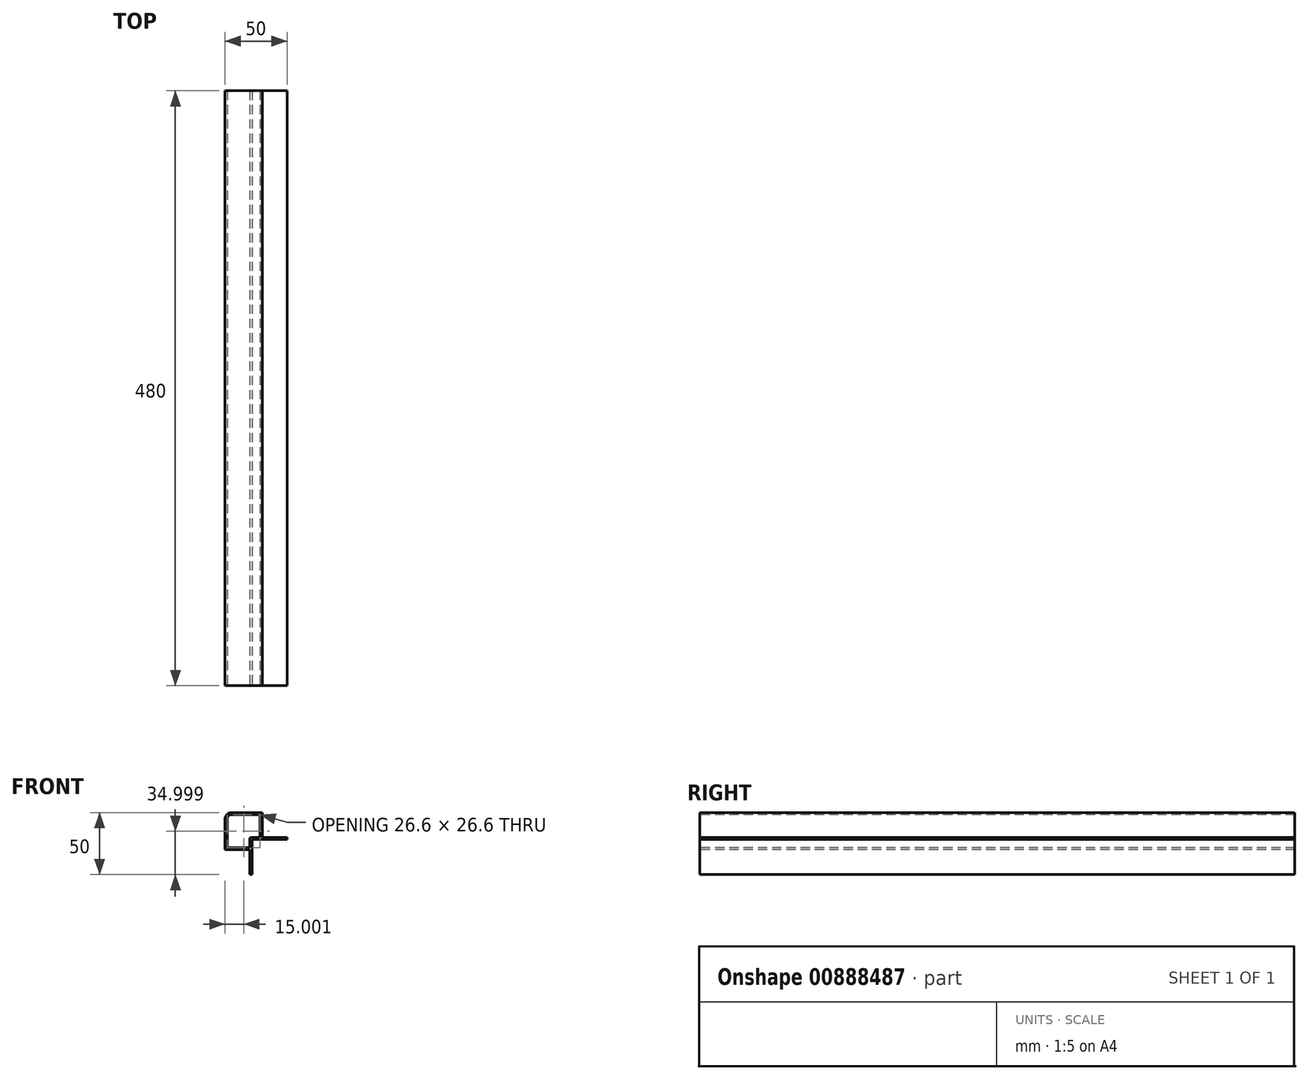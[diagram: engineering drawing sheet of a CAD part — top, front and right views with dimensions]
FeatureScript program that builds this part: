
annotation { "Feature Type Name" : "Feature", "Feature Type Description" : "" }
export const myFeature = defineFeature(function(context is Context, id is Id, definition is map)
    precondition{}
    {
        {
            var Q0;
            Q0=qCreatedBy(makeId("Front.planeOp"),FACE);
            var sketch = newSketch(context, id + "F0", { "sketchPlane" : qUnion([Q0])});
            skLineSegment(sketch, "E0.bottom", {"start": v(-14.05, 19.05) * mm, "end": v(10.95, 19.05) * mm});
            skLineSegment(sketch, "E0.top", {"start": v(-19.05, -10.95) * mm, "end": v(0.95, -10.95) * mm});
            skLineSegment(sketch, "E0.left", {"start": v(-19.05, 14.05) * mm, "end": v(-19.05, -10.95) * mm});
            skLineSegment(sketch, "E0.right", {"start": v(10.95, 19.05) * mm, "end": v(10.95, -0.95) * mm});
            skPoint(sketch, "E0.middle", {"position": v(-4.05, 4.05) * mm});
            skLineSegment(sketch, "E1", {"start": v(0.95, -1.95) * mm, "end": v(0.95, -9.25) * mm});
            skLineSegment(sketch, "E2", {"start": v(1.95, -0.95) * mm, "end": v(9.25, -0.95) * mm});
            skPoint(sketch, "E3.orphan", {"position": v(10.95, -10.95) * mm});
            skLineSegment(sketch, "E4", {"start": v(30.95, -0.95) * mm, "end": v(30.95, -2.65) * mm});
            skLineSegment(sketch, "E5", {"start": v(30.95, -2.65) * mm, "end": v(2.65, -2.65) * mm});
            skLineSegment(sketch, "E6", {"start": v(2.65, -2.65) * mm, "end": v(2.65, -30.95) * mm});
            skLineSegment(sketch, "E7", {"start": v(2.65, -30.95) * mm, "end": v(0.95, -30.95) * mm});
            skLineSegment(sketch, "E8.trimOffspring", {"start": v(10.95, -0.95) * mm, "end": v(30.95, -0.95) * mm});
            skLineSegment(sketch, "E9.trimOffspring", {"start": v(0.95, -10.95) * mm, "end": v(0.95, -30.95) * mm});
            skPoint(sketch, "E10.visualSharp", {"position": v(-19.05, 19.05) * mm});
            skArc(sketch, "E10.filletArc", {"start": v(-14.05, 19.05) * mm, "mid": v(-17.58, 17.58) * mm, "end": v(-19.05, 14.05) * mm});
            skLineSegment(sketch, "E11.0", {"start": v(-14.05, 17.35) * mm, "end": v(9.25, 17.35) * mm});
            skLineSegment(sketch, "E12.0", {"start": v(-17.35, 14.05) * mm, "end": v(-17.35, -9.25) * mm});
            skArc(sketch, "E12.1", {"start": v(-14.05, 17.35) * mm, "mid": v(-16.38, 16.38) * mm, "end": v(-17.35, 14.05) * mm});
            skLineSegment(sketch, "E13.0", {"start": v(9.25, 17.35) * mm, "end": v(9.25, -0.95) * mm});
            skLineSegment(sketch, "E14.0", {"start": v(-17.35, -9.25) * mm, "end": v(0.95, -9.25) * mm});
            skPoint(sketch, "E15.visualSharp", {"position": v(0.95, -0.95) * mm});
            skArc(sketch, "E15.filletArc", {"start": v(1.95, -0.95) * mm, "mid": v(1.24, -1.24) * mm, "end": v(0.95, -1.95) * mm});
            skSolve(sketch);
        }
        {
            var Q0;
            Q0=makeQuery(id+"F0.imprint","IMPRINT",FACE,{"disambiguationData":[TD([[makeQuery(id+"F0.imprint","IMPRINT",EDGE,{"derivedFrom":sQuery(id+"F0.wireOp",EDGE,"E0.bottom")}),-1.0]])]});
            extrude(context, id + "F1", {"entities" : qUnion([Q0]), "oppositeDirection" : true, "depth" : 480 * mm, "offsetDistance" : 25 * mm});
        }
    });
